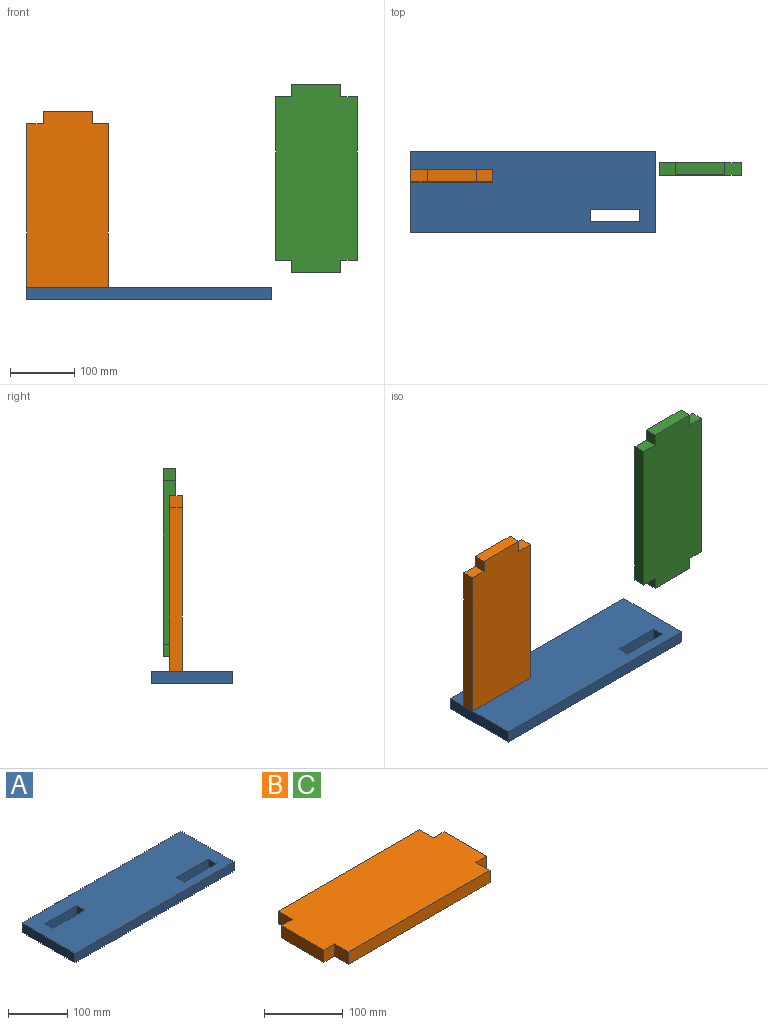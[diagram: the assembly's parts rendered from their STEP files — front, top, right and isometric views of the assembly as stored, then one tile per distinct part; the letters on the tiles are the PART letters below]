
ASSEMBLY  parts=3 mates=1
PART A: 14 faces, bbox 381x127x19.1 mm
  f0: plane 381x127mm, normal (0,0,1), area 45483.8mm2, adj f2,f3,f4,f5,f6,f7,f8,f9
  f1: plane 381x127mm, normal (0,0,-1), area 45483.8mm2, adj f2,f3,f4,f5,f6,f7,f8,f9
  f2: plane 127x19.05mm, normal (-1,0,0), area 2419.3mm2, adj f0,f1,f3,f5
  f3: plane 381x19.05mm, normal (0,-1,0), area 7258mm2, adj f0,f1,f2,f4
  f4: plane 127x19.05mm, normal (1,0,0), area 2419.3mm2, adj f0,f1,f3,f5
  f5: plane 381x19.05mm, normal (0,1,0), area 7258mm2, adj f0,f1,f2,f4
  f6: plane 76.2x19.05mm, normal (0,-1,0), area 1451.6mm2, adj f0,f1,f7,f9
  f7: plane 19.05x19.05mm, normal (1,0,0), area 362.9mm2, adj f0,f1,f6,f8
  f8: plane 76.2x19.05mm, normal (0,1,0), area 1451.6mm2, adj f0,f1,f7,f9
  f9: plane 19.05x19.05mm, normal (-1,0,0), area 362.9mm2, adj f0,f1,f6,f8
  f10: plane 76.2x19.05mm, normal (0,-1,0), area 1451.6mm2, adj f0,f1,f11,f13
  f11: plane 19.05x19.05mm, normal (1,0,0), area 362.9mm2, adj f0,f1,f10,f12
  f12: plane 76.2x19.05mm, normal (0,1,0), area 1451.6mm2, adj f0,f1,f11,f13
  f13: plane 19.05x19.05mm, normal (-1,0,0), area 362.9mm2, adj f0,f1,f10,f12
PART B: 14 faces, bbox 292.1x127x19.1 mm
  f0: plane 19.05x19.05mm, normal (0,1,0), area 362.9mm2, adj f1,f11,f12,f13
  f1: plane 76.2x19.05mm, normal (-1,0,0), area 1451.6mm2, adj f0,f2,f12,f13
  f2: plane 19.05x19.05mm, normal (0,-1,0), area 362.9mm2, adj f1,f3,f12,f13
  f3: plane 25.4x19.05mm, normal (-1,0,0), area 483.9mm2, adj f2,f4,f12,f13
  f4: plane 254x19.05mm, normal (0,-1,0), area 4838.7mm2, adj f3,f5,f12,f13
  f5: plane 25.4x19.05mm, normal (1,0,0), area 483.9mm2, adj f4,f6,f12,f13
  f6: plane 19.05x19.05mm, normal (0,-1,0), area 362.9mm2, adj f5,f7,f12,f13
  f7: plane 76.2x19.05mm, normal (1,0,0), area 1451.6mm2, adj f6,f8,f12,f13
  f8: plane 19.05x19.05mm, normal (0,1,0), area 362.9mm2, adj f7,f9,f12,f13
  f9: plane 25.4x19.05mm, normal (1,0,0), area 483.9mm2, adj f8,f10,f12,f13
  f10: plane 254x19.05mm, normal (0,1,0), area 4838.7mm2, adj f9,f11,f12,f13
  f11: plane 25.4x19.05mm, normal (-1,0,0), area 483.9mm2, adj f0,f10,f12,f13
  f12: plane 292.1x127mm, normal (0,0,1), area 35161.2mm2, adj f0,f1,f2,f3,f4,f5,f6,f7
  f13: plane 292.1x127mm, normal (0,0,-1), area 35161.2mm2, adj f0,f1,f2,f3,f4,f5,f6,f7
PART C: same geometry as B
PLACE A t=(-201.28,100.12,-11.36)mm
PLACE B rot(axis=(0.58,-0.58,0.58),120deg) t=(-175.46,174.48,81.5)mm
PLACE C rot(axis=(0.58,0.58,-0.58),120deg) t=(168.19,184.99,229.68)mm
MATE fastened A.f0 <-> B.f11  axis (0,0,1) through (-235.11,174.48,7.69)mm
